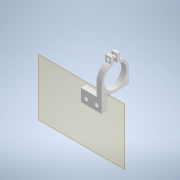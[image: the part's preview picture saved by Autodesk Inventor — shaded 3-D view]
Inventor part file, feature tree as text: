
AUTODESK INVENTOR PART (.ipt)
format: ipt  version: 2022 (Build 260153000, 153)  size: 160,768 bytes
history: native  units: mm
features: other x4, extrude x3, sketch x3, plane x1, reference x1, projected_geometry x1
ambient origin geometry x8: Origin, YZ Plane, XZ Plane, XY Plane, X Axis, Y Axis, Z Axis, Center Point
bodies: Solid1 (feature_tree)
feature tree (13):
  plane  "Work Plane1"
  extrude  "Extrusion1"  Depth=5.0mm
  extrude  "Extrusion2"  Depth=5.0mm
  extrude  "Extrusion3"  Depth=26.0mm
  sketch  "Sketch1"  dims[d0=5.0mm d1=5.0mm]
  reference  "Reference1"
  sketch  "Sketch2"  dims[d2=5.0mm d3=0.1mm]
  sketch  "Sketch3"  dims[d4=5.0mm d5=0.0mm d6=26.0mm d7=26.0mm d8=21.3mm d9=3.0mm d10=3.0mm d11=5.0mm d12=5.0mm d13=0.0mm d14=3.3mm d15=0.0mm d16=0.0mm]
  projected_geometry  "Projected Loop1"
  other  "<userpath>\OneDrive - Imperial College London\ROBOICP\Final Assembly\Final Assembly.iam"
  other  "Final Assembly.iam"
  other  "Solids Feeder Head Assembly:1"
  other  "body:1"
